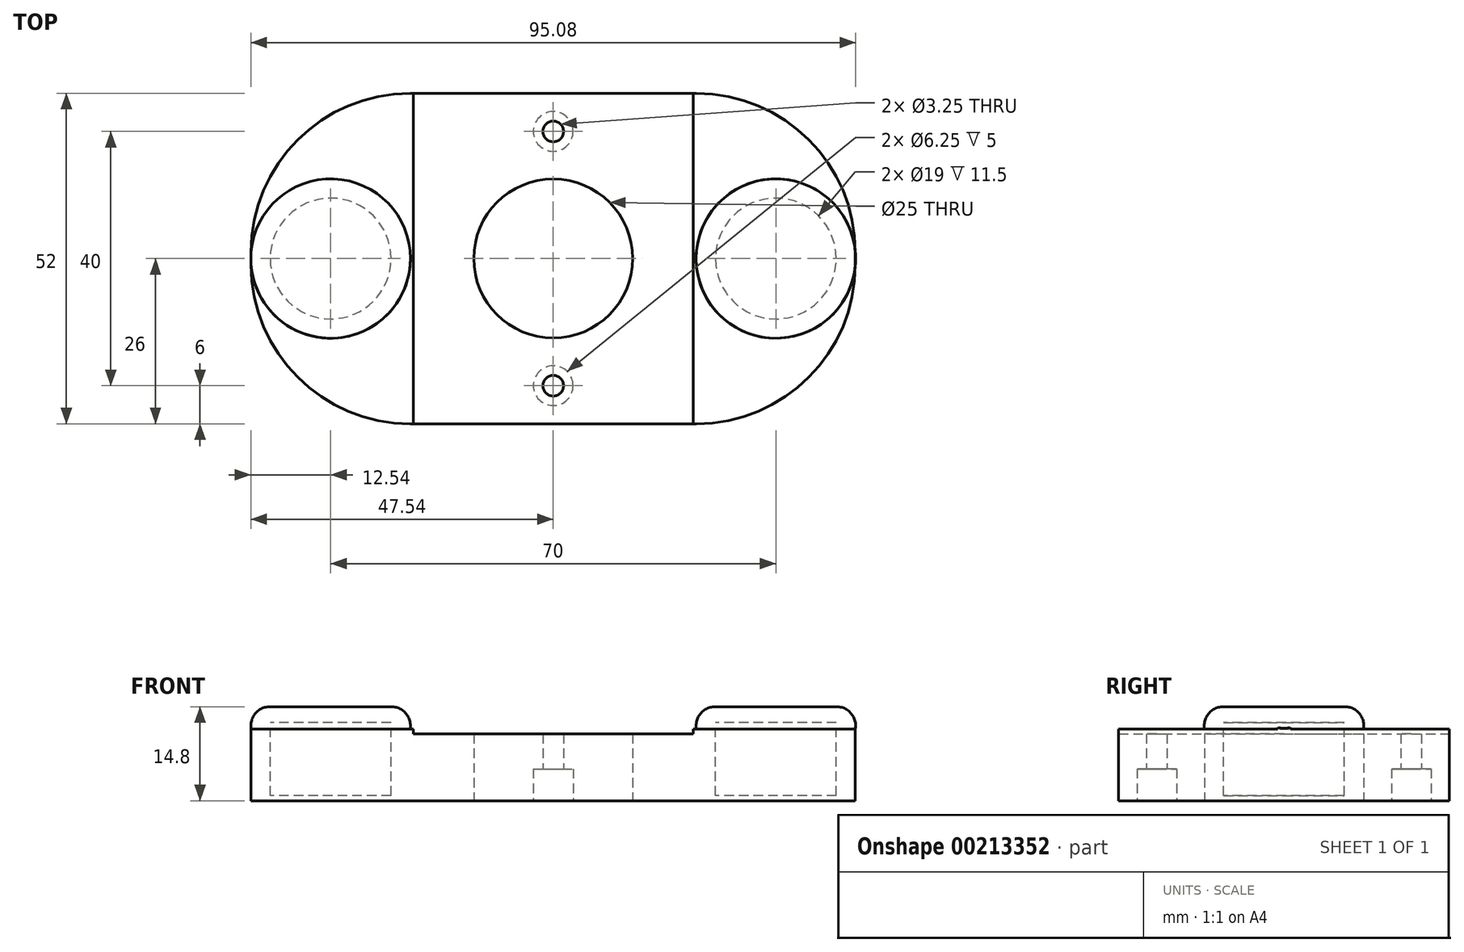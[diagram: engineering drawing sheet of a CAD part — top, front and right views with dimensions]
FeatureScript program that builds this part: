
annotation { "Feature Type Name" : "Feature", "Feature Type Description" : "" }
export const myFeature = defineFeature(function(context is Context, id is Id, definition is map)
    precondition{}
    {
        {
            var Q0;
            Q0=qCreatedBy(makeId("Top.planeOp"),FACE);
            var sketch = newSketch(context, id + "F0", { "sketchPlane" : qUnion([Q0])});
            skLineSegment(sketch, "E0.bottom", {"start": v(22.5, -26) * mm, "end": v(-22.5, -26) * mm});
            skLineSegment(sketch, "E0.top", {"start": v(22.5, 26) * mm, "end": v(-22.5, 26) * mm});
            skLineSegment(sketch, "E0.left", {"start": v(47.5, -1) * mm, "end": v(47.5, 1) * mm});
            skLineSegment(sketch, "E0.right", {"start": v(-47.5, -1) * mm, "end": v(-47.5, 1) * mm});
            skPoint(sketch, "E0.middle", {"position": v(0, 0) * mm});
            skPoint(sketch, "E1.visualSharp", {"position": v(-47.5, 26) * mm});
            skArc(sketch, "E1.filletArc", {"start": v(-22.5, 26) * mm, "mid": v(-40.18, 18.68) * mm, "end": v(-47.5, 1) * mm});
            skPoint(sketch, "E2.visualSharp", {"position": v(-47.5, -26) * mm});
            skArc(sketch, "E2.filletArc", {"start": v(-47.5, -1) * mm, "mid": v(-40.18, -18.68) * mm, "end": v(-22.5, -26) * mm});
            skPoint(sketch, "E3.visualSharp", {"position": v(47.5, -26) * mm});
            skArc(sketch, "E3.filletArc", {"start": v(22.5, -26) * mm, "mid": v(40.18, -18.68) * mm, "end": v(47.5, -1) * mm});
            skPoint(sketch, "E4.visualSharp", {"position": v(47.5, 26) * mm});
            skArc(sketch, "E4.filletArc", {"start": v(47.5, 1) * mm, "mid": v(40.18, 18.68) * mm, "end": v(22.5, 26) * mm});
            skLineSegment(sketch, "E5", {"start": v(0, 0) * mm, "end": v(0, 20) * mm, "construction": true});
            skCircle(sketch, "E6", {"center": v(0, 20) * mm, "radius": 1.63 * mm});
            skLineSegment(sketch, "E7", {"start": v(0, 0) * mm, "end": v(-18.65, 0) * mm, "construction": true});
            skCircle(sketch, "E8.MirrorC", {"center": v(0, -20) * mm, "radius": 1.63 * mm});
            skSolve(sketch);
        }
        {
            var Q0;
            Q0 = qSketchRegion(id + "F0", true);
            extrude(context, id + "F1", {"entities" : qUnion([Q0]), "depth" : 11.3 * mm});
        }
        {
            var Q0;
            Q0=makeQuery(id+"F1.opExtrude","CAP_FACE",FACE,{"disambiguationData":[OSD([sQuery(id+"F0.wireOp",EDGE,"E0.bottom"),sQuery(id+"F0.wireOp",EDGE,"E0.top"),sQuery(id+"F0.wireOp",EDGE,"E0.left"),sQuery(id+"F0.wireOp",EDGE,"E0.right"),sQuery(id+"F0.wireOp",EDGE,"E1.filletArc"),sQuery(id+"F0.wireOp",EDGE,"E2.filletArc"),sQuery(id+"F0.wireOp",EDGE,"E3.filletArc"),sQuery(id+"F0.wireOp",EDGE,"E4.filletArc"),sQuery(id+"F0.wireOp",EDGE,"E6"),sQuery(id+"F0.wireOp",EDGE,"E8.MirrorC")])],"isStart":true});
            var sketch = newSketch(context, id + "F2", { "sketchPlane" : qUnion([Q0])});
            skCircle(sketch, "E9", {"center": v(0, 0) * mm, "radius": 12.5 * mm});
            skSolve(sketch);
        }
        {
            var Q0;
            Q0 = qSketchRegion(id + "F2", true);
            extrude(context, id + "F3", {"entities" : qUnion([Q0]), "operationType" : NewBodyOperationType.REMOVE, "endBound" : BoundingType.THROUGH_ALL, "oppositeDirection" : true, "depth" : 25 * mm});
        }
        {
            var Q0;
            Q0=makeQuery(id+"F1.opExtrude","CAP_FACE",FACE,{"disambiguationData":[OSD([sQuery(id+"F0.wireOp",EDGE,"E0.bottom"),sQuery(id+"F0.wireOp",EDGE,"E0.top"),sQuery(id+"F0.wireOp",EDGE,"E0.left"),sQuery(id+"F0.wireOp",EDGE,"E0.right"),sQuery(id+"F0.wireOp",EDGE,"E1.filletArc"),sQuery(id+"F0.wireOp",EDGE,"E2.filletArc"),sQuery(id+"F0.wireOp",EDGE,"E3.filletArc"),sQuery(id+"F0.wireOp",EDGE,"E4.filletArc"),sQuery(id+"F0.wireOp",EDGE,"E6"),sQuery(id+"F0.wireOp",EDGE,"E8.MirrorC")])],"isStart":false});
            var sketch = newSketch(context, id + "F4", { "sketchPlane" : qUnion([Q0])});
            skLineSegment(sketch, "E10", {"start": v(-47.5, 0) * mm, "end": v(-12.5, 0) * mm, "construction": true});
            skLineSegment(sketch, "E11", {"start": v(0, 0) * mm, "end": v(0, 5.87) * mm, "construction": true});
            skLineSegment(sketch, "E12", {"start": v(-30, 0) * mm, "end": v(-35, 0) * mm});
            skCircle(sketch, "E13", {"center": v(-35, 0) * mm, "radius": 9.5 * mm});
            skCircle(sketch, "E14.MirrorC", {"center": v(35, 0) * mm, "radius": 9.5 * mm});
            skSolve(sketch);
        }
        {
            var Q0;
            Q0 = qSketchRegion(id + "F4", true);
            extrude(context, id + "F5", {"entities" : qUnion([Q0]), "operationType" : NewBodyOperationType.REMOVE, "oppositeDirection" : true, "depth" : 10.5 * mm});
        }
        {
            var Q0;
            Q0=makeQuery(id+"F1.opExtrude","CAP_FACE",FACE,{"disambiguationData":[OSD([sQuery(id+"F0.wireOp",EDGE,"E0.bottom"),sQuery(id+"F0.wireOp",EDGE,"E0.top"),sQuery(id+"F0.wireOp",EDGE,"E0.left"),sQuery(id+"F0.wireOp",EDGE,"E0.right"),sQuery(id+"F0.wireOp",EDGE,"E1.filletArc"),sQuery(id+"F0.wireOp",EDGE,"E2.filletArc"),sQuery(id+"F0.wireOp",EDGE,"E3.filletArc"),sQuery(id+"F0.wireOp",EDGE,"E4.filletArc"),sQuery(id+"F0.wireOp",EDGE,"E6"),sQuery(id+"F0.wireOp",EDGE,"E8.MirrorC")])],"isStart":true});
            var sketch = newSketch(context, id + "F6", { "sketchPlane" : qUnion([Q0])});
            skCircle(sketch, "E15", {"center": v(0, 20) * mm, "radius": 3.12 * mm});
            skLineSegment(sketch, "E16", {"start": v(0, 0) * mm, "end": v(8.02, 0) * mm, "construction": true});
            skCircle(sketch, "E17.MirrorC", {"center": v(0, -20) * mm, "radius": 3.12 * mm});
            skSolve(sketch);
        }
        {
            var Q0;
            Q0 = qSketchRegion(id + "F6", true);
            extrude(context, id + "F7", {"entities" : qUnion([Q0]), "operationType" : NewBodyOperationType.REMOVE, "oppositeDirection" : true, "depth" : 5 * mm});
        }
        {
            var Q0;
            Q0=makeQuery(id+"F1.opExtrude","CAP_FACE",FACE,{"disambiguationData":[OSD([sQuery(id+"F0.wireOp",EDGE,"E0.bottom"),sQuery(id+"F0.wireOp",EDGE,"E0.top"),sQuery(id+"F0.wireOp",EDGE,"E0.left"),sQuery(id+"F0.wireOp",EDGE,"E0.right"),sQuery(id+"F0.wireOp",EDGE,"E1.filletArc"),sQuery(id+"F0.wireOp",EDGE,"E2.filletArc"),sQuery(id+"F0.wireOp",EDGE,"E3.filletArc"),sQuery(id+"F0.wireOp",EDGE,"E4.filletArc"),sQuery(id+"F0.wireOp",EDGE,"E6"),sQuery(id+"F0.wireOp",EDGE,"E8.MirrorC")])],"isStart":false});
            var sketch = newSketch(context, id + "F8", { "sketchPlane" : qUnion([Q0])});
            skLineSegment(sketch, "E18.bottom", {"start": v(22, -26) * mm, "end": v(-22, -26) * mm});
            skLineSegment(sketch, "E18.top", {"start": v(22, 26) * mm, "end": v(-22, 26) * mm});
            skLineSegment(sketch, "E18.left", {"start": v(22, -26) * mm, "end": v(22, 26) * mm});
            skLineSegment(sketch, "E18.right", {"start": v(-22, -26) * mm, "end": v(-22, 26) * mm});
            skPoint(sketch, "E18.middle", {"position": v(0, 0) * mm});
            skPoint(sketch, "E19", {"position": v(35, 0) * mm});
            skSolve(sketch);
        }
        {
            var Q0;
            Q0 = qSketchRegion(id + "F8", true);
            extrude(context, id + "F9", {"entities" : qUnion([Q0]), "operationType" : NewBodyOperationType.REMOVE, "oppositeDirection" : true, "depth" : .8 * mm});
        }
        {
            var Q0;
            {var subQ0=sQuery(id+"F0.wireOp",EDGE,"E1.filletArc");var subQ1=sQuery(id+"F0.wireOp",EDGE,"E0.right");var subQ2=sQuery(id+"F0.wireOp",EDGE,"E0.top");var subQ3=sQuery(id+"F0.wireOp",EDGE,"E0.bottom");var subQ4=sQuery(id+"F0.wireOp",EDGE,"E2.filletArc");Q0=makeQuery(id+"F9.boolean.opBoolean","SPLIT",FACE,{"disambiguationData":[TD([makeQuery(id+"F1.opExtrude","SWEPT_FACE",FACE,{"disambiguationData":[OSD([subQ1])]})])],"derivedFrom":makeQuery(id+"F1.opExtrude","CAP_FACE",FACE,{"disambiguationData":[OSD([subQ3,subQ2,sQuery(id+"F0.wireOp",EDGE,"E0.left"),subQ1,subQ0,subQ4,sQuery(id+"F0.wireOp",EDGE,"E3.filletArc"),sQuery(id+"F0.wireOp",EDGE,"E4.filletArc"),sQuery(id+"F0.wireOp",EDGE,"E6"),sQuery(id+"F0.wireOp",EDGE,"E8.MirrorC")])],"isStart":false})});}
            var sketch = newSketch(context, id + "F10", { "sketchPlane" : qUnion([Q0])});
            skCircle(sketch, "E20", {"center": v(-35, 0) * mm, "radius": 12.54 * mm});
            skLineSegment(sketch, "E21", {"start": v(0, 0) * mm, "end": v(0, 51.58) * mm, "construction": true});
            skCircle(sketch, "E22.MirrorC", {"center": v(35, 0) * mm, "radius": 12.54 * mm});
            skCircle(sketch, "E23", {"center": v(-35, 0) * mm, "radius": 9.5 * mm});
            skCircle(sketch, "E24", {"center": v(35, 0) * mm, "radius": 9.5 * mm});
            skSolve(sketch);
        }
        {
            var Q0;
            Q0 = qSketchRegion(id + "F10", true);
            extrude(context, id + "F11", {"entities" : qUnion([Q0]), "operationType" : NewBodyOperationType.ADD, "depth" : 1 * mm});
        }
        {
            var Q0;
            Q0=makeQuery(id+"F11.opExtrude","CAP_FACE",FACE,{"disambiguationData":[OSD([sQuery(id+"F10.wireOp",EDGE,"E20"),sQuery(id+"F10.wireOp",EDGE,"E23")])],"isStart":false});
            var sketch = newSketch(context, id + "F12", { "sketchPlane" : qUnion([Q0])});
            skCircle(sketch, "E25", {"center": v(-35, 0) * mm, "radius": 12.54 * mm});
            skLineSegment(sketch, "E26", {"start": v(0, 0) * mm, "end": v(0, 50.98) * mm});
            skLineSegment(sketch, "E27", {"start": v(0, 0) * mm, "end": v(35, 0) * mm, "construction": true});
            skCircle(sketch, "E28", {"center": v(35, 0) * mm, "radius": 12.54 * mm});
            skSolve(sketch);
        }
        {
            var Q0;
            Q0 = qSketchRegion(id + "F12", true);
            extrude(context, id + "F13", {"entities" : qUnion([Q0]), "operationType" : NewBodyOperationType.ADD, "depth" : 2.5 * mm});
        }
        {
            var Q0;
            Q0=makeQuery(id+"F13.opExtrude","CAP_EDGE",EDGE,{"disambiguationData":[OSD([sQuery(id+"F12.wireOp",EDGE,"E25")])],"isStart":false});
            fillet(context, id + "F14", {"entities" : qUnion([Q0]), "radius" : 3 * mm, "tangentPropagation" : true, "allowEdgeOverflow" : false});
        }
        {
            var Q0;
            Q0=makeQuery(id+"F13.opExtrude","CAP_EDGE",EDGE,{"disambiguationData":[OSD([sQuery(id+"F12.wireOp",EDGE,"E28")])],"isStart":false});
            fillet(context, id + "F15", {"entities" : qUnion([Q0]), "radius" : 3 * mm, "tangentPropagation" : true, "allowEdgeOverflow" : false});
        }
        {
            var Q0;
            {var subQ0=sQuery(id+"F10.wireOp",EDGE,"E20");Q0=makeQuery(id+"F11.boolean.opBoolean","SPLIT",EDGE,{"disambiguationData":[topologyDisambiguationEdgeConnected([makeQuery(id+"F1.opExtrude","CAP_FACE",FACE,{"disambiguationData":[OSD([sQuery(id+"F0.wireOp",EDGE,"E0.bottom"),sQuery(id+"F0.wireOp",EDGE,"E0.top"),sQuery(id+"F0.wireOp",EDGE,"E0.left"),sQuery(id+"F0.wireOp",EDGE,"E0.right"),sQuery(id+"F0.wireOp",EDGE,"E1.filletArc"),sQuery(id+"F0.wireOp",EDGE,"E2.filletArc"),sQuery(id+"F0.wireOp",EDGE,"E3.filletArc"),sQuery(id+"F0.wireOp",EDGE,"E4.filletArc"),sQuery(id+"F0.wireOp",EDGE,"E6"),sQuery(id+"F0.wireOp",EDGE,"E8.MirrorC")])],"isStart":false})])],"derivedFrom":makeQuery(id+"F11.opExtrude","CAP_EDGE",EDGE,{"disambiguationData":[OSD([subQ0])],"isStart":true})});}
            fillet(context, id + "F16", {"entities" : qUnion([Q0]), "radius" : .25 * mm, "tangentPropagation" : true, "allowEdgeOverflow" : false});
        }
        {
            var Q0;
            {var subQ0=sQuery(id+"F10.wireOp",EDGE,"E22.MirrorC");Q0=makeQuery(id+"F11.boolean.opBoolean","SPLIT",EDGE,{"disambiguationData":[topologyDisambiguationEdgeConnected([makeQuery(id+"F1.opExtrude","CAP_FACE",FACE,{"disambiguationData":[OSD([sQuery(id+"F0.wireOp",EDGE,"E0.bottom"),sQuery(id+"F0.wireOp",EDGE,"E0.top"),sQuery(id+"F0.wireOp",EDGE,"E0.left"),sQuery(id+"F0.wireOp",EDGE,"E0.right"),sQuery(id+"F0.wireOp",EDGE,"E1.filletArc"),sQuery(id+"F0.wireOp",EDGE,"E2.filletArc"),sQuery(id+"F0.wireOp",EDGE,"E3.filletArc"),sQuery(id+"F0.wireOp",EDGE,"E4.filletArc"),sQuery(id+"F0.wireOp",EDGE,"E6"),sQuery(id+"F0.wireOp",EDGE,"E8.MirrorC")])],"isStart":false})])],"derivedFrom":makeQuery(id+"F11.opExtrude","CAP_EDGE",EDGE,{"disambiguationData":[OSD([subQ0])],"isStart":true})});}
            fillet(context, id + "F17", {"entities" : qUnion([Q0]), "radius" : .25 * mm, "allowEdgeOverflow" : false});
        }
    });
